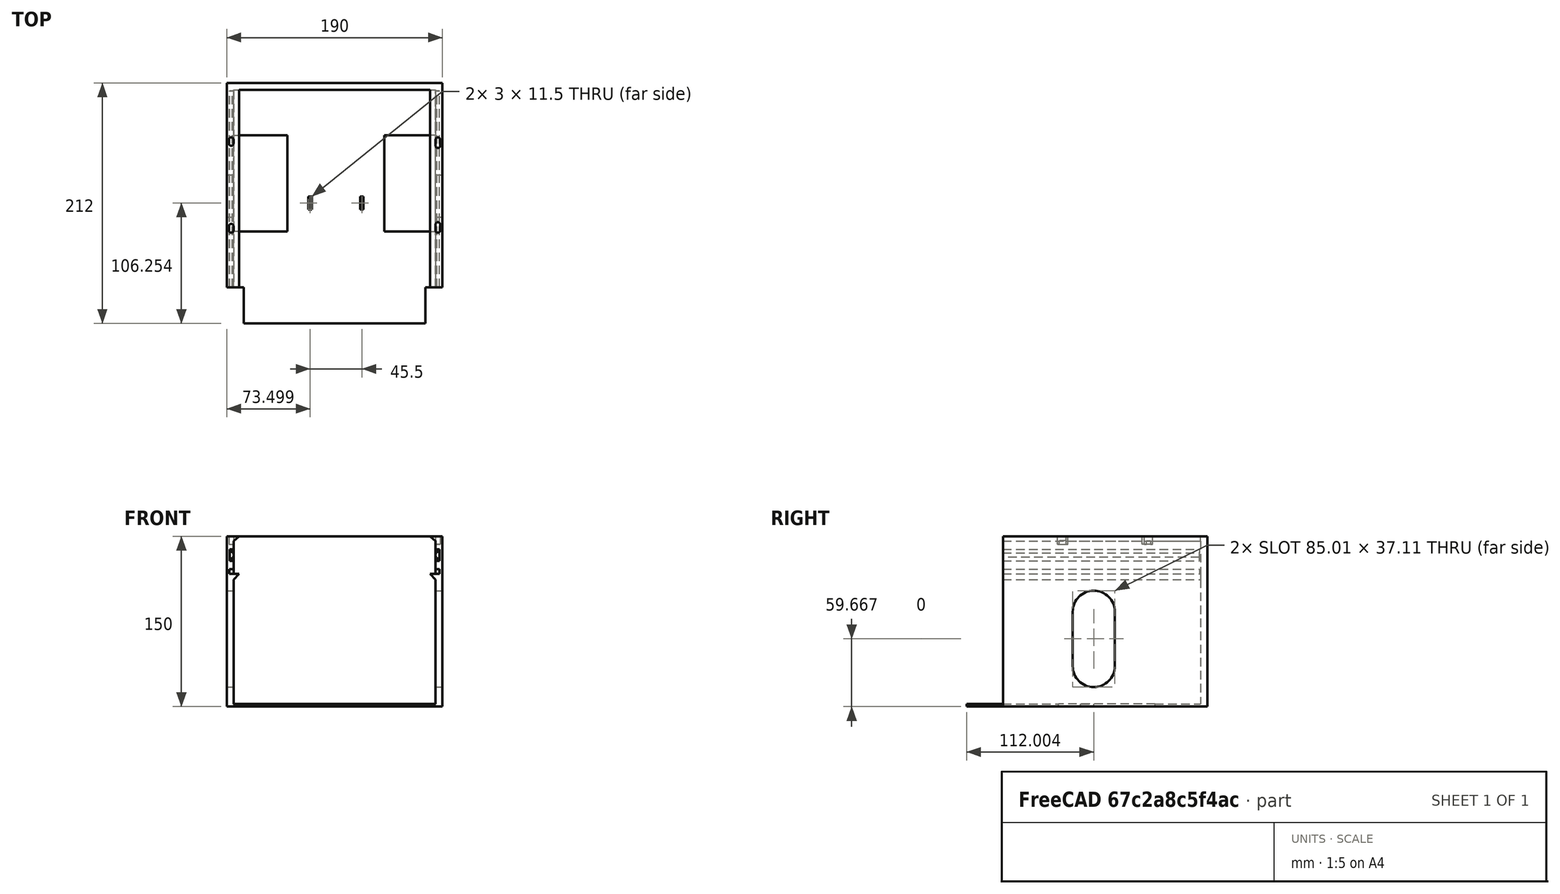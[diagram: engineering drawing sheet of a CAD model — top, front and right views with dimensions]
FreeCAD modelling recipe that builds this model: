
FCSTD DOCUMENT  (FreeCAD 0.19R)
Label: piezaprincipal
License: All rights reserved
LicenseURL: http://en.wikipedia.org/wiki/All_rights_reserved
objects: Sketcher::SketchObject×23, PartDesign::Pocket×10, PartDesign::Plane×4, PartDesign::Pad×3, App::Part×1, PartDesign::Body×1, PartDesign::Line×1
note: 55 computed .brp shape members not serialized (recipe doc carries the construction recipe); baked Part::Feature solids carry a one-line shape summary decoded from their .brp

FEATURE [Sketcher::SketchObject] Sketch
  FullyConstrained = false
  MapMode = 5
  Support = -> [XY_Plane002]
  sketch-geometry (6):
    g0: LineSegment StartX=-93.1012 StartY=-107.176 StartZ=0 EndX=96.8988 EndY=-107.176 EndZ=0
    g1: LineSegment StartX=96.8988 StartY=-107.176 StartZ=0 EndX=96.8988 EndY=112.824 EndZ=0
    g2: LineSegment StartX=96.8988 StartY=112.824 StartZ=0 EndX=-93.1012 EndY=112.824 EndZ=0
    g3: LineSegment StartX=-93.1012 StartY=112.824 StartZ=0 EndX=-93.1012 EndY=-107.176 EndZ=0
    g4: LineSegment StartX=-93.1012 StartY=-107.176 StartZ=0 EndX=0 EndY=0 EndZ=0
    g5: LineSegment StartX=3.79761 StartY=5.64841 StartZ=0 EndX=96.8988 EndY=112.824 EndZ=0
  constraints (15):
    c: Coincident(g0,g1)
    c: Coincident(g1,g2)
    c: Coincident(g2,g3)
    c: Coincident(g3,g0)
    c: Horizontal(g0)
    c: Horizontal(g2)
    c: Vertical(g1)
    c: Vertical(g3)
    c: DistanceY(g1,g1) = 220
    c: DistanceX(g0,g0) = 190
    c: Coincident(g4,g0)
    c: Coincident(g4,g-1)
    c: Coincident(g5,g1)
    c: Equal(g4,g5)
    c: Parallel(g4,g5)
FEATURE [PartDesign::Pad] Pad
  Direction = (1,1,1)
  Length = 150
  Length2 = 100
  Profile = -> Sketch
  Refine = true
  Type = 0
FEATURE [Sketcher::SketchObject] Sketch001
  ExternalGeometry = -> [Pad]
  FullyConstrained = false
  MapMode = 5
  Placement = pos=(0,0,150) rot=(0,0,1;0rad)
  Support = -> [Pad]
  sketch-geometry (8):
    g0: LineSegment StartX=-87.1012 StartY=106.824 StartZ=0 EndX=90.8988 EndY=106.824 EndZ=0
    g1: LineSegment StartX=90.8988 StartY=106.824 StartZ=0 EndX=90.8988 EndY=-101.176 EndZ=0
    g2: LineSegment StartX=90.8988 StartY=-101.176 StartZ=0 EndX=-87.1012 EndY=-101.176 EndZ=0
    g3: LineSegment StartX=-87.1012 StartY=-101.176 StartZ=0 EndX=-87.1012 EndY=106.824 EndZ=0
    g4: LineSegment StartX=-93.1012 StartY=98.9099 StartZ=0 EndX=-87.1012 EndY=98.9099 EndZ=0
    g5: LineSegment StartX=-75.3955 StartY=106.824 StartZ=0 EndX=-75.3955 EndY=112.824 EndZ=0
    g6: LineSegment StartX=76.7175 StartY=-101.176 StartZ=0 EndX=76.7175 EndY=-107.176 EndZ=0
    g7: LineSegment StartX=90.8988 StartY=-90.9586 StartZ=0 EndX=96.8988 EndY=-90.9586 EndZ=0
  constraints (24):
    c: Coincident(g0,g1)
    c: Coincident(g1,g2)
    c: Coincident(g2,g3)
    c: Coincident(g3,g0)
    c: Horizontal(g0)
    c: Horizontal(g2)
    c: Vertical(g1)
    c: Vertical(g3)
    c: PointOnObject(g4,g-4)
    c: PointOnObject(g4,g3)
    c: Horizontal(g4)
    c: PointOnObject(g5,g0)
    c: PointOnObject(g5,g-3)
    c: Vertical(g5)
    c: DistanceX(g4,g4) = 6
    c: DistanceY(g5,g5) = 6
    c: PointOnObject(g6,g2)
    c: PointOnObject(g6,g-6)
    c: Vertical(g6)
    c: PointOnObject(g7,g1)
    c: PointOnObject(g7,g-5)
    c: Horizontal(g7)
    c: DistanceY(g6,g6) = 6
    c: DistanceX(g7,g7) = 6
FEATURE [PartDesign::Pocket] Pocket
  BaseFeature = -> Pad
  Length = 147.5
  Length2 = 100
  Profile = -> Sketch001
  Refine = true
  Type = 0
FEATURE [Sketcher::SketchObject] Sketch002
  ExternalGeometry = -> [Pocket]
  FullyConstrained = true
  MapMode = 5
  Placement = pos=(0,0,0) rot=(1,0,0;3.14159rad)
  Support = -> [Pocket]
  sketch-geometry (16):
    g0: LineSegment StartX=-93.1012 StartY=-66.8242 StartZ=0 EndX=-87.1012 EndY=-66.8242 EndZ=0
    g1: LineSegment StartX=-87.1012 StartY=-66.8242 StartZ=0 EndX=-39.6012 EndY=-66.8242 EndZ=0
    g2: LineSegment StartX=-39.6012 StartY=-66.8242 StartZ=0 EndX=-39.6012 EndY=-106.824 EndZ=0
    g3: LineSegment StartX=-39.6012 StartY=-106.824 StartZ=0 EndX=-39.6012 EndY=-112.824 EndZ=0
    g4: LineSegment StartX=45.8988 StartY=-112.824 StartZ=0 EndX=45.8988 EndY=-106.824 EndZ=0
    g5: LineSegment StartX=45.8988 StartY=-106.824 StartZ=0 EndX=45.8988 EndY=-66.8242 EndZ=0
    g6: LineSegment StartX=45.8988 StartY=-66.8242 StartZ=0 EndX=90.8988 EndY=-66.8242 EndZ=0
    g7: LineSegment StartX=90.8988 StartY=-66.8242 StartZ=0 EndX=96.8988 EndY=-66.8242 EndZ=0
    g8: LineSegment StartX=90.8988 StartY=-66.8242 StartZ=0 EndX=45.8988 EndY=-66.8242 EndZ=0
    g9: LineSegment StartX=45.8988 StartY=-66.8242 StartZ=0 EndX=45.8988 EndY=18.1758 EndZ=0
    g10: LineSegment StartX=45.8988 StartY=18.1758 StartZ=0 EndX=90.8988 EndY=18.1758 EndZ=0
    g11: LineSegment StartX=90.8988 StartY=18.1758 StartZ=0 EndX=90.8988 EndY=-66.8242 EndZ=0
    g12: LineSegment StartX=-87.1012 StartY=-66.8242 StartZ=0 EndX=-39.6012 EndY=-66.8242 EndZ=0
    g13: LineSegment StartX=-39.6012 StartY=-66.8242 StartZ=0 EndX=-39.6012 EndY=18.1758 EndZ=0
    g14: LineSegment StartX=-39.6012 StartY=18.1758 StartZ=0 EndX=-87.1012 EndY=18.1758 EndZ=0
    g15: LineSegment StartX=-87.1012 StartY=18.1758 StartZ=0 EndX=-87.1012 EndY=-66.8242 EndZ=0
  constraints (48):
    c: PointOnObject(g0,g-4)
    c: Horizontal(g0)
    c: DistanceX(g0,g0) = 6
    c: Coincident(g1,g0)
    c: Horizontal(g1)
    c: DistanceX(g1,g1) = 47.5
    c: Coincident(g2,g1)
    c: Vertical(g2)
    c: DistanceY(g2,g2) = 40
    c: Coincident(g3,g2)
    c: PointOnObject(g3,g-6)
    c: Vertical(g3)
    c: DistanceY(g3,g3) = 6
    c: PointOnObject(g4,g-6)
    c: Vertical(g4)
    c: DistanceY(g4,g4) = 6
    c: Coincident(g5,g4)
    c: Vertical(g5)
    c: DistanceY(g5,g5) = 40
    c: Coincident(g6,g5)
    c: Horizontal(g6)
    c: DistanceX(g6,g6) = 45
    c: Coincident(g7,g6)
    c: PointOnObject(g7,g-5)
    c: Horizontal(g7)
    c: DistanceX(g7,g7) = 6
    c: Coincident(g8,g9)
    c: Coincident(g9,g10)
    c: Coincident(g10,g11)
    c: Coincident(g11,g8)
    c: Horizontal(g8)
    c: Horizontal(g10)
    c: Vertical(g9)
    c: Vertical(g11)
    c: Coincident(g8,g6)
    c: Coincident(g12,g13)
    c: Coincident(g13,g14)
    c: Coincident(g14,g15)
    c: Coincident(g15,g12)
    c: Horizontal(g12)
    c: Horizontal(g14)
    c: Vertical(g13)
    c: Vertical(g15)
    c: Coincident(g12,g0)
    c: DistanceY(g13,g13) = 85
    c: DistanceY(g9,g9) = 85
    c: DistanceX(g14,g14) = 47.5
    c: DistanceX(g10,g10) = 45
FEATURE [PartDesign::Pocket] Pocket001
  BaseFeature = -> Pocket
  Length = 100
  Length2 = 100
  Profile = -> Sketch002
  Refine = true
  Type = 0
FEATURE [Sketcher::SketchObject] Sketch003
  ExternalGeometry = -> [Pocket001]
  FullyConstrained = true
  MapMode = 5
  Placement = pos=(0,0,0) rot=(1,0,0;3.14159rad)
  Support = -> [Pocket001]
  sketch-geometry (12):
    g0: LineSegment StartX=-21.1012 StartY=-112.824 StartZ=0 EndX=-21.1012 EndY=-12.8242 EndZ=0
    g1: LineSegment StartX=-21.1012 StartY=-12.8242 StartZ=0 EndX=-39.6012 EndY=-12.8242 EndZ=0
    g2: LineSegment StartX=45.8988 StartY=-12.8242 StartZ=0 EndX=27.3988 EndY=-12.8242 EndZ=0
    g3: LineSegment StartX=27.3988 StartY=-12.8242 StartZ=0 EndX=27.3988 EndY=-112.824 EndZ=0
    g4: LineSegment StartX=-21.1012 StartY=-12.8242 StartZ=0 EndX=-18.1012 EndY=-12.8242 EndZ=0
    g5: LineSegment StartX=-18.1012 StartY=-12.8242 StartZ=0 EndX=-18.1012 EndY=-1.3242 EndZ=0
    g6: LineSegment StartX=-18.1012 StartY=-1.3242 StartZ=0 EndX=-21.1012 EndY=-1.3242 EndZ=0
    g7: LineSegment StartX=-21.1012 StartY=-1.3242 StartZ=0 EndX=-21.1012 EndY=-12.8242 EndZ=0
    g8: LineSegment StartX=27.3988 StartY=-12.8242 StartZ=0 EndX=24.3988 EndY=-12.8242 EndZ=0
    g9: LineSegment StartX=24.3988 StartY=-12.8242 StartZ=0 EndX=24.3988 EndY=-1.3242 EndZ=0
    g10: LineSegment StartX=24.3988 StartY=-1.3242 StartZ=0 EndX=27.3988 EndY=-1.3242 EndZ=0
    g11: LineSegment StartX=27.3988 StartY=-1.3242 StartZ=0 EndX=27.3988 EndY=-12.8242 EndZ=0
  constraints (36):
    c: PointOnObject(g0,g-3)
    c: Vertical(g0)
    c: DistanceY(g0,g0) = 100
    c: Coincident(g1,g0)
    c: PointOnObject(g1,g-10)
    c: Horizontal(g1)
    c: DistanceX(g1,g1) = 18.5
    c: PointOnObject(g2,g-7)
    c: Horizontal(g2)
    c: Coincident(g3,g2)
    c: PointOnObject(g3,g-3)
    c: Vertical(g3)
    c: DistanceX(g2,g2) = 18.5
    c: DistanceY(g3,g3) = 100
    c: Coincident(g4,g5)
    c: Coincident(g5,g6)
    c: Coincident(g6,g7)
    c: Coincident(g7,g4)
    c: Horizontal(g4)
    c: Horizontal(g6)
    c: Vertical(g5)
    c: Vertical(g7)
    c: Coincident(g4,g0)
    c: Coincident(g8,g9)
    c: Coincident(g9,g10)
    c: Coincident(g10,g11)
    c: Coincident(g11,g8)
    c: Horizontal(g8)
    c: Horizontal(g10)
    c: Vertical(g9)
    c: Vertical(g11)
    c: Coincident(g8,g2)
    c: DistanceX(g4,g4) = 3
    c: DistanceX(g10,g10) = 3
    c: DistanceY(g5,g5) = 11.5
    c: DistanceY(g9,g9) = 11.5
FEATURE [PartDesign::Pocket] Pocket002
  BaseFeature = -> Pocket001
  Length = 100
  Length2 = 100
  Profile = -> Sketch003
  Refine = true
  Type = 0
FEATURE [Sketcher::SketchObject] Sketch004
  ExternalGeometry = -> [Pocket002]
  FullyConstrained = true
  MapMode = 5
  Placement = pos=(0,0,0) rot=(1,0,0;3.14159rad)
  Support = -> [Pocket002]
  sketch-geometry (8):
    g0: LineSegment StartX=-93.1012 StartY=107.176 StartZ=0 EndX=-78.1012 EndY=107.176 EndZ=0
    g1: LineSegment StartX=-78.1012 StartY=107.176 StartZ=0 EndX=-78.1012 EndY=67.1758 EndZ=0
    g2: LineSegment StartX=-78.1012 StartY=67.1758 StartZ=0 EndX=-93.1012 EndY=67.1758 EndZ=0
    g3: LineSegment StartX=-93.1012 StartY=67.1758 StartZ=0 EndX=-93.1012 EndY=107.176 EndZ=0
    g4: LineSegment StartX=96.8988 StartY=107.176 StartZ=0 EndX=81.8988 EndY=107.176 EndZ=0
    g5: LineSegment StartX=81.8988 StartY=107.176 StartZ=0 EndX=81.8988 EndY=67.1758 EndZ=0
    g6: LineSegment StartX=81.8988 StartY=67.1758 StartZ=0 EndX=96.8988 EndY=67.1758 EndZ=0
    g7: LineSegment StartX=96.8988 StartY=67.1758 StartZ=0 EndX=96.8988 EndY=107.176 EndZ=0
  constraints (22):
    c: Coincident(g0,g1)
    c: Coincident(g1,g2)
    c: Coincident(g2,g3)
    c: Coincident(g3,g0)
    c: Horizontal(g0)
    c: Horizontal(g2)
    c: Vertical(g1)
    c: Vertical(g3)
    c: Coincident(g0,g-4)
    c: Coincident(g4,g5)
    c: Coincident(g5,g6)
    c: Coincident(g6,g7)
    c: Coincident(g7,g4)
    c: Horizontal(g4)
    c: Horizontal(g6)
    c: Vertical(g5)
    c: Vertical(g7)
    c: Coincident(g4,g-5)
    c: DistanceY(g1,g1) = 40
    c: DistanceX(g2,g2) = 15
    c: DistanceX(g6,g6) = 15
    c: DistanceY(g5,g5) = 40
FEATURE [PartDesign::Pocket] Pocket003
  BaseFeature = -> Pocket002
  Length = 150
  Length2 = 100
  Profile = -> Sketch004
  Refine = true
  Type = 0
FEATURE [Sketcher::SketchObject] Sketch005
  ExternalGeometry = -> [Pocket003]
  FullyConstrained = false
  MapMode = 5
  Placement = pos=(0,0,0) rot=(1,0,0;3.14159rad)
  Support = -> [Pocket003]
  sketch-geometry (5):
    g0: LineSegment StartX=-99.2298 StartY=126.087 StartZ=0 EndX=94.8409 EndY=126.087 EndZ=0
    g1: LineSegment StartX=94.8409 StartY=126.087 StartZ=0 EndX=94.8409 EndY=99.1758 EndZ=0
    g2: LineSegment StartX=94.8409 StartY=99.1758 StartZ=0 EndX=-99.2298 EndY=99.1758 EndZ=0
    g3: LineSegment StartX=-99.2298 StartY=99.1758 StartZ=0 EndX=-99.2298 EndY=126.087 EndZ=0
    g4: LineSegment StartX=-22.0404 StartY=107.176 StartZ=0 EndX=-22.0404 EndY=99.1758 EndZ=0
  constraints (12):
    c: Coincident(g0,g1)
    c: Coincident(g1,g2)
    c: Coincident(g2,g3)
    c: Coincident(g3,g0)
    c: Horizontal(g0)
    c: Horizontal(g2)
    c: Vertical(g1)
    c: Vertical(g3)
    c: PointOnObject(g4,g-4)
    c: PointOnObject(g4,g2)
    c: Vertical(g4)
    c: DistanceY(g4,g4) = 8
FEATURE [PartDesign::Pocket] Pocket004
  BaseFeature = -> Pocket003
  Length = 5
  Length2 = 100
  Profile = -> Sketch005
  Refine = true
  Type = 1
FEATURE [PartDesign::Plane] DatumPlane
  Length = 211.469
  MapMode = 2
  Placement = pos=(0,0,0) rot=(0.57735,0.57735,0.57735;4.18879rad)
  ResizeMode = 0
  Support = -> [Z_Axis001]
  Width = 226.469
FEATURE [PartDesign::Plane] DatumPlane001
  Length = 226.469
  MapMode = 5
  Placement = pos=(0,-67.1758,0) rot=(1,0,0;1.5708rad)
  ResizeMode = 0
  Support = -> [Pocket004]
  Width = 211.469
FEATURE [Sketcher::SketchObject] Sketch006
  ExternalGeometry = -> [Pocket004]
  FullyConstrained = false
  MapMode = 5
  Placement = pos=(0,-67.1758,0) rot=(1,0,0;1.5708rad)
  Support = -> [DatumPlane001]
  sketch-geometry (17):
    g0: LineSegment StartX=94.3988 StartY=150 StartZ=0 EndX=94.3988 EndY=146 EndZ=0
    g1: LineSegment StartX=94.3988 StartY=146 StartZ=0 EndX=94.3988 EndY=121 EndZ=0
    g2: LineSegment StartX=94.3988 StartY=149.811 StartZ=0 EndX=90.8988 EndY=149.811 EndZ=0
    g3: LineSegment StartX=94.3988 StartY=121 StartZ=0 EndX=95.4282 EndY=121 EndZ=0
    g4: LineSegment StartX=95.4282 StartY=121 StartZ=0 EndX=95.4282 EndY=133.5 EndZ=0
    g5: LineSegment StartX=94.3988 StartY=128.507 StartZ=0 EndX=91.9634 EndY=128.507 EndZ=0
    g6: LineSegment StartX=91.9634 StartY=128.507 StartZ=0 EndX=91.9634 EndY=138.507 EndZ=0
    g7: LineSegment StartX=91.9634 StartY=138.507 StartZ=0 EndX=94.3988 EndY=138.507 EndZ=0
    g8: LineSegment StartX=94.3988 StartY=138.507 StartZ=0 EndX=94.3988 EndY=128.507 EndZ=0
    g9: LineSegment StartX=90.8988 StartY=136.069 StartZ=0 EndX=91.9634 EndY=136.069 EndZ=0
    g10: LineSegment StartX=90.8988 StartY=135.397 StartZ=0 EndX=94.3988 EndY=135.397 EndZ=0
    g11: LineSegment StartX=-90.6012 StartY=138.507 StartZ=0 EndX=-88.2012 EndY=138.507 EndZ=0
    g12: LineSegment StartX=-88.2012 StartY=138.507 StartZ=0 EndX=-88.2012 EndY=128.507 EndZ=0
    g13: LineSegment StartX=-88.2012 StartY=128.507 StartZ=0 EndX=-90.6012 EndY=128.507 EndZ=0
    g14: LineSegment StartX=-90.6012 StartY=128.507 StartZ=0 EndX=-90.6012 EndY=138.507 EndZ=0
    g15: LineSegment StartX=-88.2012 StartY=137.428 StartZ=0 EndX=-87.1012 EndY=137.428 EndZ=0
    g16: LineSegment StartX=-87.1012 StartY=134.229 StartZ=0 EndX=-90.6012 EndY=134.229 EndZ=0
  constraints (47):
    c: PointOnObject(g0,g-9)
    c: Vertical(g0)
    c: DistanceY(g0,g0) = 4
    c: Coincident(g1,g0)
    c: Vertical(g1)
    c: PointOnObject(g2,g0)
    c: PointOnObject(g2,g-7)
    c: Horizontal(g2)
    c: DistanceX(g2,g2) = 3.5
    c: Coincident(g3,g1)
    c: Horizontal(g3)
    c: Coincident(g4,g3)
    c: Vertical(g4)
    c: DistanceY(g4,g4) = 12.5
    c: Coincident(g5,g6)
    c: Coincident(g6,g7)
    c: Coincident(g7,g8)
    c: Coincident(g8,g5)
    c: Horizontal(g5)
    c: Horizontal(g7)
    c: Vertical(g6)
    c: Vertical(g8)
    c: PointOnObject(g5,g1)
    c: DistanceY(g8,g8) = 10
    c: PointOnObject(g9,g-7)
    c: PointOnObject(g9,g6)
    c: Horizontal(g9)
    c: PointOnObject(g10,g-7)
    c: PointOnObject(g10,g8)
    c: Horizontal(g10)
    c: Coincident(g11,g12)
    c: Coincident(g12,g13)
    c: Coincident(g13,g14)
    c: Coincident(g14,g11)
    c: Horizontal(g11)
    c: Horizontal(g13)
    c: Vertical(g12)
    c: Vertical(g14)
    c: PointOnObject(g15,g12)
    c: PointOnObject(g15,g-4)
    c: Horizontal(g15)
    c: DistanceX(g15,g15) = 1.1
    c: PointOnObject(g16,g-4)
    c: PointOnObject(g16,g14)
    c: Horizontal(g16)
    c: DistanceX(g16,g16) = 3.5
    c: DistanceY(g5,g5) = 0
FEATURE [PartDesign::Pocket] Pocket005
  BaseFeature = -> Pocket004
  Length = 173
  Length2 = 100
  Profile = -> Sketch006
  Refine = true
  Type = 0
FEATURE [Sketcher::SketchObject] Sketch007
  ExternalGeometry = -> [Pocket005]
  FullyConstrained = false
  MapMode = 5
  Placement = pos=(0,-67.1758,0) rot=(1,0,0;1.5708rad)
  Support = -> [DatumPlane001]
  sketch-geometry (13):
    g0: LineSegment StartX=-89.9246 StartY=150 StartZ=0 EndX=-89.9246 EndY=138.507 EndZ=0
    g1: LineSegment StartX=-89.2841 StartY=135.507 StartZ=0 EndX=-85.86 EndY=135.507 EndZ=0
    g2: LineSegment StartX=-85.86 StartY=135.507 StartZ=0 EndX=-85.86 EndY=131.507 EndZ=0
    g3: LineSegment StartX=-85.86 StartY=131.507 StartZ=0 EndX=-89.2841 EndY=131.507 EndZ=0
    g4: LineSegment StartX=-89.2841 StartY=131.507 StartZ=0 EndX=-89.2841 EndY=135.507 EndZ=0
    g5: LineSegment StartX=89.2537 StartY=135.507 StartZ=0 EndX=93.0882 EndY=135.507 EndZ=0
    g6: LineSegment StartX=93.0882 StartY=135.507 StartZ=0 EndX=93.0882 EndY=131.507 EndZ=0
    g7: LineSegment StartX=93.0882 StartY=131.507 StartZ=0 EndX=89.2537 EndY=131.507 EndZ=0
    g8: LineSegment StartX=89.2537 StartY=131.507 StartZ=0 EndX=89.2537 EndY=135.507 EndZ=0
    g9: LineSegment StartX=-88.9726 StartY=135.507 StartZ=0 EndX=-88.9726 EndY=138.507 EndZ=0
    g10: LineSegment StartX=-89.081 StartY=128.507 StartZ=0 EndX=-89.081 EndY=131.507 EndZ=0
    g11: LineSegment StartX=92.5435 StartY=135.507 StartZ=0 EndX=92.5435 EndY=138.507 EndZ=0
    g12: LineSegment StartX=92.5535 StartY=131.507 StartZ=0 EndX=92.5535 EndY=128.507 EndZ=0
  constraints (36):
    c: PointOnObject(g0,g-11)
    c: PointOnObject(g0,g-9)
    c: Vertical(g0)
    c: DistanceX(g-10,g-10) = 2.4
    c: Coincident(g1,g2)
    c: Coincident(g2,g3)
    c: Coincident(g3,g4)
    c: Coincident(g4,g1)
    c: Horizontal(g1)
    c: Horizontal(g3)
    c: Vertical(g2)
    c: Vertical(g4)
    c: Coincident(g5,g6)
    c: Coincident(g6,g7)
    c: Coincident(g7,g8)
    c: Coincident(g8,g5)
    c: Horizontal(g5)
    c: Horizontal(g7)
    c: Vertical(g6)
    c: Vertical(g8)
    c: DistanceY(g2,g2) = 4
    c: DistanceY(g8,g8) = 4
    c: PointOnObject(g9,g1)
    c: PointOnObject(g9,g-9)
    c: Vertical(g9)
    c: PointOnObject(g10,g-10)
    c: PointOnObject(g10,g3)
    c: Vertical(g10)
    c: Equal(g9,g10)
    c: PointOnObject(g11,g5)
    c: PointOnObject(g11,g-8)
    c: Vertical(g11)
    c: PointOnObject(g12,g7)
    c: PointOnObject(g12,g-7)
    c: Vertical(g12)
    c: Equal(g12,g11)
FEATURE [PartDesign::Pocket] Pocket006
  BaseFeature = -> Pocket005
  Length = 173
  Length2 = 100
  Profile = -> Sketch007
  Refine = true
  Type = 0
FEATURE [Sketcher::SketchObject] Sketch008
  ExternalGeometry = -> [Pocket006]
  FullyConstrained = false
  MapMode = 5
  Placement = pos=(0,-67.1758,0) rot=(1,0,0;1.5708rad)
  Support = -> [DatumPlane001]
  sketch-geometry (14):
    g0: LineSegment StartX=94.5227 StartY=150 StartZ=0 EndX=94.5227 EndY=146 EndZ=0
    g1: LineSegment StartX=94.5227 StartY=146 StartZ=0 EndX=90.8988 EndY=146 EndZ=0
    g2: LineSegment StartX=92.9315 StartY=138.507 StartZ=0 EndX=92.9315 EndY=146 EndZ=0
    g3: LineSegment StartX=-89.849 StartY=150 StartZ=0 EndX=-89.849 EndY=146 EndZ=0
    g4: LineSegment StartX=-89.849 StartY=146 StartZ=0 EndX=-89.849 EndY=138.507 EndZ=0
    g5: LineSegment StartX=94.3988 StartY=128.507 StartZ=0 EndX=94.3988 EndY=121.007 EndZ=0
    g6: LineSegment StartX=94.3988 StartY=121.007 StartZ=0 EndX=90.8988 EndY=121.007 EndZ=0
    g7: LineSegment StartX=90.8988 StartY=121.007 StartZ=0 EndX=90.8988 EndY=117.007 EndZ=0
    g8: LineSegment StartX=94.3988 StartY=121.007 StartZ=0 EndX=-90.6545 EndY=121.007 EndZ=0
    g9: LineSegment StartX=-90.6545 StartY=121.007 StartZ=0 EndX=-90.6545 EndY=117.007 EndZ=0
    g10: LineSegment StartX=-90.6545 StartY=117.007 StartZ=0 EndX=94.3988 EndY=117.007 EndZ=0
    g11: LineSegment StartX=94.3988 StartY=117.007 StartZ=0 EndX=94.3988 EndY=121.007 EndZ=0
    g12: LineSegment StartX=-87.1545 StartY=118.932 StartZ=0 EndX=-90.6545 EndY=118.932 EndZ=0
    g13: LineSegment StartX=90.8988 StartY=120.1 StartZ=0 EndX=94.3988 EndY=120.1 EndZ=0
  constraints (41):
    c: PointOnObject(g0,g-7)
    c: Vertical(g0)
    c: DistanceY(g0,g0) = 4
    c: Coincident(g1,g0)
    c: PointOnObject(g1,g-11)
    c: Horizontal(g1)
    c: PointOnObject(g2,g-9)
    c: PointOnObject(g2,g1)
    c: Vertical(g2)
    c: PointOnObject(g3,g-5)
    c: Vertical(g3)
    c: DistanceY(g3,g3) = 4
    c: Coincident(g4,g3)
    c: PointOnObject(g4,g-4)
    c: Vertical(g4)
    c: DistanceY(g-3,g-3) = 10
    c: Coincident(g5,g-14)
    c: Vertical(g5)
    c: DistanceY(g5,g5) = 7.5
    c: Coincident(g6,g5)
    c: PointOnObject(g6,g-15)
    c: Horizontal(g6)
    c: Coincident(g7,g6)
    c: PointOnObject(g7,g-15)
    c: DistanceY(g7,g7) = 4
    c: Coincident(g8,g9)
    c: Coincident(g9,g10)
    c: Coincident(g10,g11)
    c: Coincident(g11,g8)
    c: Horizontal(g8)
    c: Horizontal(g10)
    c: Vertical(g9)
    c: Vertical(g11)
    c: Coincident(g8,g5)
    c: DistanceY(g9,g9) = 4
    c: PointOnObject(g12,g9)
    c: Horizontal(g12)
    c: DistanceX(g12,g12) = 3.5
    c: PointOnObject(g13,g7)
    c: PointOnObject(g13,g11)
    c: Horizontal(g13)
FEATURE [PartDesign::Pocket] Pocket007
  BaseFeature = -> Pocket006
  Length = 173
  Length2 = 100
  Profile = -> Sketch008
  Refine = true
  Type = 0
FEATURE [Sketcher::SketchObject] Sketch009
  ExternalGeometry = -> [Pocket007]
  FullyConstrained = true
  MapMode = 5
  Placement = pos=(0,-67.1758,0) rot=(1,0,0;1.5708rad)
  Support = -> [DatumPlane001]
  sketch-geometry (6):
    g0: LineSegment StartX=-87.1012 StartY=117.007 StartZ=0 EndX=-82.1012 EndY=117.007 EndZ=0
    g1: LineSegment StartX=-87.1012 StartY=117.007 StartZ=0 EndX=-87.1012 EndY=112.007 EndZ=0
    g2: LineSegment StartX=-87.1012 StartY=112.007 StartZ=0 EndX=-82.1012 EndY=117.007 EndZ=0
    g3: LineSegment StartX=90.8988 StartY=117.007 StartZ=0 EndX=85.8988 EndY=117.007 EndZ=0
    g4: LineSegment StartX=90.8988 StartY=117.007 StartZ=0 EndX=90.8988 EndY=112.007 EndZ=0
    g5: LineSegment StartX=85.8988 StartY=117.007 StartZ=0 EndX=90.8988 EndY=112.007 EndZ=0
  constraints (16):
    c: Coincident(g0,g-4)
    c: Horizontal(g0)
    c: DistanceX(g0,g0) = 5
    c: Coincident(g1,g0)
    c: PointOnObject(g1,g-3)
    c: DistanceY(g1,g1) = 5
    c: Coincident(g2,g1)
    c: Coincident(g2,g0)
    c: Coincident(g3,g-6)
    c: Horizontal(g3)
    c: Coincident(g4,g3)
    c: PointOnObject(g4,g-6)
    c: Coincident(g5,g3)
    c: Coincident(g5,g4)
    c: DistanceX(g3,g3) = 5
    c: DistanceY(g4,g4) = 5
FEATURE [PartDesign::Pad] Pad001
  BaseFeature = -> Pocket007
  Direction = (1,1,1)
  Length = 10
  Length2 = 100
  Profile = -> Sketch009
  Refine = true
  Type = 3
  UpToFace = -> Pocket007 [Face50]
FEATURE [Sketcher::SketchObject] Sketch010
  ExternalGeometry = -> [Pad001]
  FullyConstrained = true
  MapMode = 5
  Placement = pos=(0,0,0) rot=(1,0,0;3.14159rad)
  Support = -> [Pad001]
  constraints (3):
    c: DistanceY(g-4,g-4) = 180
    c: DistanceY(g-3,g-3) = 0
    c: DistanceX(g-3,g-3) = 190
FEATURE [Sketcher::SketchObject] Sketch011
  ExternalGeometry = -> [Pad001]
  FullyConstrained = true
  MapMode = 5
  Placement = pos=(0,-67.1758,0) rot=(1,0,0;1.5708rad)
  Support = -> [DatumPlane001]
  sketch-geometry (9):
    g0: LineSegment StartX=-87.1012 StartY=150 StartZ=0 EndX=-87.1012 EndY=146 EndZ=0
    g1: LineSegment StartX=90.8988 StartY=150 StartZ=0 EndX=90.8988 EndY=146 EndZ=0
    g2: LineSegment StartX=90.8988 StartY=146 StartZ=0 EndX=90.8988 EndY=121 EndZ=0
    g3: LineSegment StartX=-87.1012 StartY=150 StartZ=0 EndX=-82.1012 EndY=150 EndZ=0
    g4: LineSegment StartX=-87.1012 StartY=150 StartZ=0 EndX=-87.1012 EndY=146 EndZ=0
    g5: LineSegment StartX=-82.1012 StartY=150 StartZ=0 EndX=-87.1012 EndY=146 EndZ=0
    g6: LineSegment StartX=90.8988 StartY=150 StartZ=0 EndX=90.8988 EndY=146 EndZ=0
    g7: LineSegment StartX=90.8988 StartY=150 StartZ=0 EndX=85.8988 EndY=150 EndZ=0
    g8: LineSegment StartX=85.8988 StartY=150 StartZ=0 EndX=90.8988 EndY=146 EndZ=0
  constraints (23):
    c: Coincident(g0,g-4)
    c: PointOnObject(g0,g-4)
    c: DistanceY(g0,g0) = 4
    c: Coincident(g1,g-6)
    c: PointOnObject(g1,g-6)
    c: DistanceY(g1,g1) = 4
    c: Coincident(g2,g1)
    c: Vertical(g2)
    c: DistanceY(g2,g2) = 25
    c: Coincident(g3,g0)
    c: Horizontal(g3)
    c: Coincident(g4,g3)
    c: Coincident(g4,g0)
    c: Coincident(g5,g3)
    c: Coincident(g5,g4)
    c: Coincident(g6,g1)
    c: Coincident(g6,g1)
    c: Coincident(g7,g6)
    c: Horizontal(g7)
    c: Coincident(g8,g7)
    c: Coincident(g8,g6)
    c: DistanceX(g7,g7) = 5
    c: DistanceX(g3,g3) = 5
FEATURE [PartDesign::Pad] Pad002
  BaseFeature = -> Pad001
  Direction = (1,1,1)
  Length = 0
  Length2 = 100
  Profile = -> Sketch011
  Refine = true
  Type = 3
  UpToFace = -> Pad001 [Face47]
FEATURE [PartDesign::Plane] DatumPlane002
  Length = 230.14
  MapMode = 2
  ResizeMode = 0
  Support = -> [X_Axis001]
  Width = 252.14
FEATURE [PartDesign::Plane] DatumPlane003
  Length = 230.14
  MapMode = 5
  Placement = pos=(0,6e-15,150) rot=(0,0,1;0rad)
  ResizeMode = 0
  Support = -> [Pad002]
  Width = 252.14
FEATURE [Sketcher::SketchObject] Sketch012
  FullyConstrained = true
  MapMode = 5
  Placement = pos=(0,6e-15,150) rot=(0,0,1;0rad)
  Support = -> [DatumPlane003]
FEATURE [Sketcher::SketchObject] Sketch013
  ExternalGeometry = -> [Pad002,DatumPlane001]
  FullyConstrained = false
  MapMode = 5
  Placement = pos=(0,6e-15,150) rot=(0,0,1;0rad)
  Support = -> [DatumPlane003]
  sketch-geometry (26):
    g0: LineSegment StartX=-93.1012 StartY=62.8242 StartZ=0 EndX=-89.1012 EndY=62.8242 EndZ=0
    g1: LineSegment StartX=-89.1012 StartY=62.8242 StartZ=0 EndX=-89.1012 EndY=112.824 EndZ=0
    g2: ArcOfCircle CenterX=-89.1012 CenterY=62.8242 CenterZ=0 NormalX=0 NormalY=0 NormalZ=1 AngleXU=0 Radius=2.00284 StartAngle=-9e-16 EndAngle=3.14159
    g3: ArcOfCircle CenterX=-89.1012 CenterY=59.4151 CenterZ=0 NormalX=0 NormalY=0 NormalZ=1 AngleXU=0 Radius=2.00284 StartAngle=3.14159 EndAngle=6.28319
    g4: LineSegment StartX=-91.104 StartY=62.8242 StartZ=0 EndX=-91.104 EndY=59.4151 EndZ=0
    g5: LineSegment StartX=-87.0984 StartY=62.8242 StartZ=0 EndX=-87.0984 EndY=59.4151 EndZ=0
    g6: LineSegment StartX=-91.104 StartY=61.3958 StartZ=0 EndX=-87.0984 EndY=61.3958 EndZ=0
    g7: LineSegment StartX=-91.104 StartY=61.956 StartZ=0 EndX=-93.1012 EndY=61.956 EndZ=0
    g8: LineSegment StartX=-93.1012 StartY=-67.1758 StartZ=0 EndX=-89.1012 EndY=-67.1758 EndZ=0
    g9: LineSegment StartX=-89.1012 StartY=-67.1758 StartZ=0 EndX=-89.1012 EndY=-17.1758 EndZ=0
    g10: ArcOfCircle CenterX=-89.1012 CenterY=-17.1758 CenterZ=0 NormalX=0 NormalY=0 NormalZ=1 AngleXU=0 Radius=1.9955 StartAngle=3.14159 EndAngle=6.28319
    g11: ArcOfCircle CenterX=-89.1012 CenterY=-13.409 CenterZ=0 NormalX=0 NormalY=0 NormalZ=1 AngleXU=0 Radius=1.9955 StartAngle=0 EndAngle=3.14159
    g12: LineSegment StartX=-87.1057 StartY=-17.1758 StartZ=0 EndX=-87.1057 EndY=-13.409 EndZ=0
    g13: LineSegment StartX=-91.0967 StartY=-17.1758 StartZ=0 EndX=-91.0967 EndY=-13.409 EndZ=0
    g14: LineSegment StartX=96.8988 StartY=112.824 StartZ=0 EndX=92.8988 EndY=112.824 EndZ=0
    g15: LineSegment StartX=92.8988 StartY=112.824 StartZ=0 EndX=92.8988 EndY=62.8242 EndZ=0
    g16: LineSegment StartX=96.8988 StartY=-67.1758 StartZ=0 EndX=92.8988 EndY=-67.1758 EndZ=0
    g17: LineSegment StartX=92.8988 StartY=-67.1758 StartZ=0 EndX=92.8988 EndY=-17.1758 EndZ=0
    g18: ArcOfCircle CenterX=92.8988 CenterY=-17.1758 CenterZ=0 NormalX=0 NormalY=0 NormalZ=1 AngleXU=0 Radius=2.03987 StartAngle=3.14159 EndAngle=6.28319
    g19: ArcOfCircle CenterX=92.8988 CenterY=-11.9746 CenterZ=0 NormalX=0 NormalY=0 NormalZ=1 AngleXU=0 Radius=2.03987 StartAngle=0 EndAngle=3.14159
    g20: LineSegment StartX=94.9387 StartY=-17.1758 StartZ=0 EndX=94.9387 EndY=-11.9746 EndZ=0
    g21: LineSegment StartX=90.8589 StartY=-17.1758 StartZ=0 EndX=90.8589 EndY=-11.9746 EndZ=0
    g22: ArcOfCircle CenterX=92.8988 CenterY=62.8242 CenterZ=0 NormalX=0 NormalY=0 NormalZ=1 AngleXU=0 Radius=1.99728 StartAngle=1e-16 EndAngle=3.14159
    g23: ArcOfCircle CenterX=92.8988 CenterY=57.4256 CenterZ=0 NormalX=0 NormalY=0 NormalZ=1 AngleXU=0 Radius=1.99728 StartAngle=3.14159 EndAngle=6.28319
    g24: LineSegment StartX=90.9015 StartY=62.8242 StartZ=0 EndX=90.9015 EndY=57.4256 EndZ=0
    g25: LineSegment StartX=94.8961 StartY=62.8242 StartZ=0 EndX=94.8961 EndY=57.4256 EndZ=0
  constraints (60):
    c: PointOnObject(g0,g-6)
    c: Horizontal(g0)
    c: DistanceX(g0,g0) = 4
    c: Coincident(g1,g0)
    c: PointOnObject(g1,g-9)
    c: Vertical(g1)
    c: DistanceY(g1,g1) = 50
    c: Tangent(g2,g5) = 1.5708
    c: Tangent(g2,g4) = -1.5708
    c: Tangent(g4,g3) = -1.5708
    c: Tangent(g5,g3) = 1.5708
    c: Vertical(g4)
    c: Equal(g2,g3)
    c: Coincident(g2,g0)
    c: PointOnObject(g6,g4)
    c: PointOnObject(g6,g5)
    c: Horizontal(g6)
    c: DistanceX(g-6,g-6) = 0
    c: PointOnObject(g7,g4)
    c: PointOnObject(g7,g-6)
    c: Horizontal(g7)
    c: Coincident(g8,g-7)
    c: PointOnObject(g8,g-8)
    c: DistanceX(g8,g8) = 4
    c: Coincident(g9,g8)
    c: Vertical(g9)
    c: DistanceY(g9,g9) = 50
    c: Tangent(g10,g13) = 1.5708
    c: Tangent(g10,g12) = -1.5708
    c: Tangent(g12,g11) = -1.5708
    c: Tangent(g13,g11) = 1.5708
    c: Vertical(g12)
    c: Equal(g10,g11)
    c: Coincident(g10,g9)
    c: Coincident(g14,g-9)
    c: PointOnObject(g14,g-9)
    c: Coincident(g15,g14)
    c: Vertical(g15)
    c: DistanceX(g14,g14) = 4
    c: DistanceY(g15,g15) = 50
    c: Coincident(g16,g-4)
    c: PointOnObject(g16,g-8)
    c: DistanceX(g16,g16) = 4
    c: Coincident(g17,g16)
    c: Vertical(g17)
    c: DistanceY(g17,g17) = 50
    c: Tangent(g18,g21) = 1.5708
    c: Tangent(g18,g20) = -1.5708
    c: Tangent(g20,g19) = -1.5708
    c: Tangent(g21,g19) = 1.5708
    c: Vertical(g20)
    c: Equal(g18,g19)
    c: Coincident(g18,g17)
    c: Tangent(g22,g25) = 1.5708
    c: Tangent(g22,g24) = -1.5708
    c: Tangent(g24,g23) = -1.5708
    c: Tangent(g25,g23) = 1.5708
    c: Vertical(g24)
    c: Equal(g22,g23)
    c: Coincident(g22,g15)
FEATURE [PartDesign::Pocket] Pocket008
  BaseFeature = -> Pad002
  Length = 7
  Length2 = 100
  Profile = -> Sketch013
  Refine = true
  Type = 0
FEATURE [Sketcher::SketchObject] Sketch014
  ExternalGeometry = -> [Pocket008]
  FullyConstrained = true
  MapMode = 5
  Placement = pos=(0,-67.1758,0) rot=(1,0,0;1.5708rad)
  Support = -> [DatumPlane001]
  sketch-geometry (1):
    g0: LineSegment StartX=-87.1012 StartY=131.507 StartZ=0 EndX=-87.1012 EndY=135.507 EndZ=0
  constraints (7):
    c: DistanceX(g-4,g-4) = 1.1
    c: Coincident(g0,g-4)
    c: Coincident(g0,g-3)
    c: DistanceY(g-7,g-7) = 3
    c: DistanceY(g-5,g-5) = 0
    c: DistanceX(g-5,g-5) = 2.4
    c: DistanceY(g-6,g-6) = 10
FEATURE [Sketcher::SketchObject] Sketch015
  ExternalGeometry = -> [Pocket008]
  FullyConstrained = true
  MapMode = 5
  Placement = pos=(0,-67.1758,0) rot=(1,0,0;1.5708rad)
  Support = -> [DatumPlane001]
  sketch-geometry (1):
    g0: LineSegment StartX=-90.6545 StartY=121.007 StartZ=0 EndX=94.3988 EndY=121.007 EndZ=0
  constraints (3):
    c: DistanceY(g-3,g-3) = 4
    c: Coincident(g0,g-3)
    c: Coincident(g0,g-4)
FEATURE [Sketcher::SketchObject] Sketch016
  ExternalGeometry = -> [Pocket008]
  FullyConstrained = true
  MapMode = 5
  Placement = pos=(0,6e-15,150) rot=(0,0,1;0rad)
  Support = -> [DatumPlane003]
  constraints (1):
    c: DistanceY(g-3,g-3) = 174
FEATURE [Sketcher::SketchObject] Sketch017
  FullyConstrained = true
  MapMode = 5
  Support = -> [DatumPlane002]
FEATURE [Sketcher::SketchObject] Sketch018
  ExternalGeometry = -> [Pocket008]
  FullyConstrained = true
  MapMode = 5
  Placement = pos=(0,0,0) rot=(1,0,0;3.14159rad)
  Support = -> [Pocket008]
  sketch-geometry (1):
    g0: LineSegment StartX=-21.1012 StartY=-12.8242 StartZ=0 EndX=-21.1012 EndY=-112.824 EndZ=0
  constraints (3):
    c: Coincident(g0,g-3)
    c: PointOnObject(g0,g-5)
    c: Vertical(g0)
FEATURE [Sketcher::SketchObject] Sketch019
  ExternalGeometry = -> [Pocket008]
  FullyConstrained = false
  MapMode = 5
  Placement = pos=(96.8988,0,0) rot=(0.57735,0.57735,0.57735;2.0944rad)
  Support = -> [Pocket008]
  sketch-geometry (5):
    g0: LineSegment StartX=112.824 StartY=35.7184 StartZ=0 EndX=12.8242 EndY=35.7184 EndZ=0
    g1: ArcOfCircle CenterX=12.8242 CenterY=35.7184 CenterZ=0 NormalX=0 NormalY=0 NormalZ=1 AngleXU=0 Radius=18.5574 StartAngle=3.14159 EndAngle=6.28319
    g2: ArcOfCircle CenterX=12.8242 CenterY=83.6151 CenterZ=0 NormalX=0 NormalY=0 NormalZ=1 AngleXU=0 Radius=18.5574 StartAngle=0 EndAngle=3.14159
    g3: LineSegment StartX=31.3816 StartY=35.7184 StartZ=0 EndX=31.3816 EndY=83.6151 EndZ=0
    g4: LineSegment StartX=-5.73323 StartY=35.7184 StartZ=0 EndX=-5.73323 EndY=83.6151 EndZ=0
  constraints (10):
    c: PointOnObject(g0,g-3)
    c: Horizontal(g0)
    c: DistanceX(g0,g0) = 100
    c: Tangent(g1,g4) = 1.5708
    c: Tangent(g1,g3) = -1.5708
    c: Tangent(g3,g2) = -1.5708
    c: Tangent(g4,g2) = 1.5708
    c: Vertical(g3)
    c: Equal(g1,g2)
    c: Coincident(g1,g0)
FEATURE [PartDesign::Pocket] Pocket009
  BaseFeature = -> Pocket008
  Length = 200
  Length2 = 100
  Profile = -> Sketch019
  Refine = true
  Type = 0
FEATURE [Sketcher::SketchObject] Sketch020
  FullyConstrained = true
  MapMode = 5
  Placement = pos=(0,-67.1758,0) rot=(1,0,0;1.5708rad)
  Support = -> [DatumPlane001]
FEATURE [Sketcher::SketchObject] Sketch021
  ExternalGeometry = -> [Pocket009]
  FullyConstrained = true
  MapMode = 5
  Placement = pos=(0,-67.1758,0) rot=(1,0,0;1.5708rad)
  Support = -> [DatumPlane001]
  sketch-geometry (1):
    g0: LineSegment StartX=-87.1012 StartY=131.507 StartZ=0 EndX=90.8988 EndY=131.507 EndZ=0
  constraints (2):
    c: Coincident(g0,g-3)
    c: Coincident(g0,g-4)
FEATURE [Sketcher::SketchObject] Sketch022
  ExternalGeometry = -> [Pocket009]
  FullyConstrained = false
  MapMode = 5
  Placement = pos=(0,6e-15,150) rot=(0,0,1;0rad)
  Support = -> [DatumPlane003]
  sketch-geometry (5):
    g0: LineSegment StartX=-89.1012 StartY=62.8242 StartZ=0 EndX=-89.1012 EndY=112.824 EndZ=0
    g1: LineSegment StartX=-87.0984 StartY=61.0758 StartZ=0 EndX=-82.1012 EndY=61.0758 EndZ=0
    g2: LineSegment StartX=-91.104 StartY=61.2037 StartZ=0 EndX=-93.2591 EndY=61.2037 EndZ=0
    g3: LineSegment StartX=-89.1012 StartY=59.4151 StartZ=0 EndX=-89.1012 EndY=-13.409 EndZ=0
    g4: LineSegment StartX=-91.0967 StartY=-13.409 StartZ=0 EndX=-87.1057 EndY=-13.409 EndZ=0
  constraints (17):
    c: DistanceY(g-3,g-3) = 0
    c: DistanceX(g-3,g-3) = 190
    c: DistanceY(g-4,g-4) = 180
    c: Coincident(g0,g-8)
    c: PointOnObject(g0,g-3)
    c: Vertical(g0)
    c: DistanceY(g-10,g-10) = 3.40905
    c: Distance(g-9) = 3.40905
    c: PointOnObject(g1,g-9)
    c: PointOnObject(g1,g-12)
    c: Horizontal(g1)
    c: PointOnObject(g2,g-10)
    c: Horizontal(g2)
    c: Coincident(g3,g-5)
    c: Coincident(g3,g-6)
    c: Coincident(g4,g-6)
    c: Coincident(g4,g-6)
FEATURE [App::Part] Part001
  Group = -> [Body]
  Origin = -> Origin001
FEATURE [PartDesign::Body] Body
  Group = -> [Sketch,Pad,Sketch001,Pocket,Sketch002,Pocket001,Sketch003,Pocket002,Sketch004,Pocket003,Sketch005,Pocket004,DatumPlane,DatumPlane001,Sketch006,Pocket005,DatumLine,Sketch007,Pocket006,Sketch008,Pocket007,Sketch009,Pad001,Sketch010,Sketch011,Pad002,DatumPlane002,DatumPlane003,Sketch012,Sketch013,Pocket008,Sketch014,Sketch015,Sketch016,Sketch017,Sketch018,Sketch019,Pocket009,Sketch020,Sketch021,+1 more]
  Origin = -> Origin002
  Tip = -> Pocket009
FEATURE [PartDesign::Line] DatumLine
  AttacherType = Attacher::AttachEngineLine
  Length = 20
  MapMode = 16
  Placement = pos=(0,0,0) rot=(0.57735,0.57735,0.57735;2.0944rad)
  ResizeMode = 0
  Support = -> [Part001]
